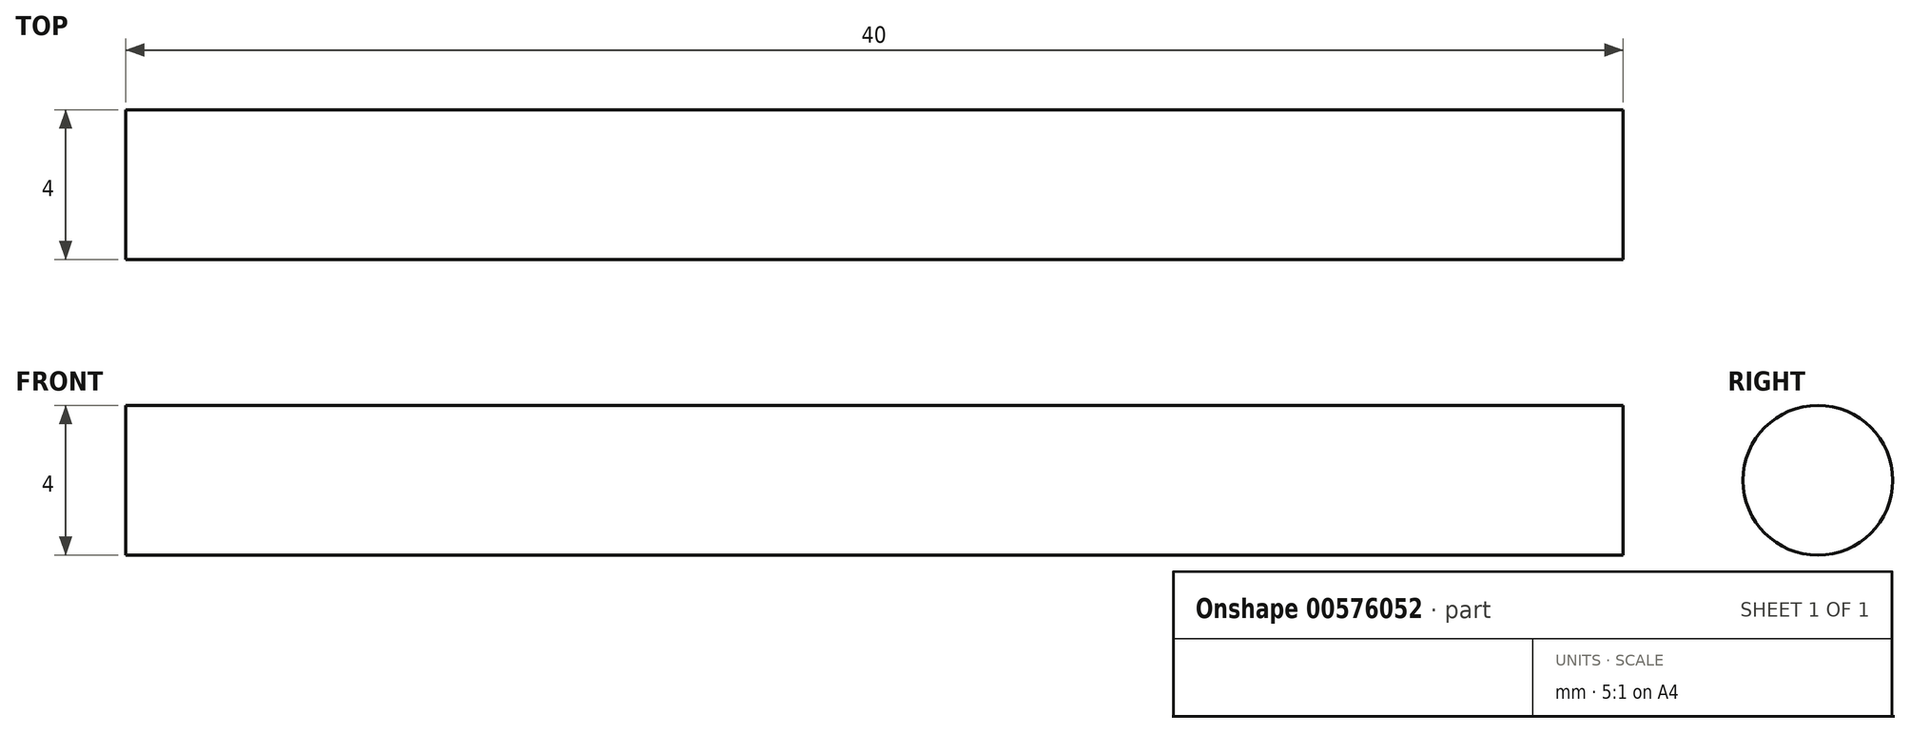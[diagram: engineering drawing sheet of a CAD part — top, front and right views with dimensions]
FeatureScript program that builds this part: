
annotation { "Feature Type Name" : "Feature", "Feature Type Description" : "" }
export const myFeature = defineFeature(function(context is Context, id is Id, definition is map)
    precondition{}
    {
        {
            var Q0;
            Q0=qCreatedBy(makeId("Right.planeOp"),FACE);
            var sketch = newSketch(context, id + "F0", { "sketchPlane" : qUnion([Q0])});
            skCircle(sketch, "E0", {"center": v(0, 0) * mm, "radius": 2 * mm});
            skSolve(sketch);
        }
        {
            var Q0;
            Q0=makeQuery(id+"F0.imprint","IMPRINT",FACE,{"disambiguationData":[TD([[makeQuery(id+"F0.imprint","IMPRINT",EDGE,{"derivedFrom":sQuery(id+"F0.wireOp",EDGE,"E0")}),1.0]])]});
            extrude(context, id + "F1", {"entities" : qUnion([Q0]), "endBound" : BoundingType.SYMMETRIC, "depth" : 40 * mm, "offsetDistance" : 25 * mm});
        }
    });
